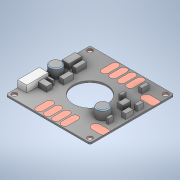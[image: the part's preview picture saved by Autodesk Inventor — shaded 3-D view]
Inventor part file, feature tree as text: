
AUTODESK INVENTOR PART (.ipt)
format: ipt  version: 2020 (Build 240168000, 168)  size: 288,256 bytes
history: mixed  units: in
note: dims shown in document units (in); Inventor stores cm internally (conversion verified against a paired STEP export)
features: other x13, chamfer x6, fillet x2, imported_body x1
ambient origin geometry x8: Origin, YZ Plane, XZ Plane, XY Plane, X Axis, Y Axis, Z Axis, Center Point
bodies: Solid1 (imported_parasolid), Solid2 (imported_parasolid), Solid3 (imported_parasolid), Solid4 (imported_parasolid), Solid5 (imported_parasolid), Solid6 (imported_parasolid), Solid7 (imported_parasolid), Solid8 (imported_parasolid), Solid9 (imported_parasolid), Solid10 (imported_parasolid), Solid11 (imported_parasolid), Solid12 (imported_parasolid), Solid13 (imported_parasolid), Solid14 (imported_parasolid), Solid15 (imported_parasolid), Solid16 (imported_parasolid), Solid17 (imported_parasolid), Solid18 (imported_parasolid), Solid19 (imported_parasolid), Solid20 (imported_parasolid), Solid21 (imported_parasolid)
feature tree (22):
  other  "Split Line4"
  fillet  "Fillet2"  [1 undecoded]
  fillet  "Fillet3"  [1 undecoded]
  other  "Boss-Extrude4[1]"
  other  "Boss-Extrude4[2]"
  other  "Boss-Extrude4[3]"
  other  "Boss-Extrude4[4]"
  other  "Boss-Extrude4[5]"
  other  "Boss-Extrude4[6]"
  other  "Boss-Extrude4[7]"
  other  "Boss-Extrude4[8]"
  other  "Boss-Extrude4[9]"
  other  "Boss-Extrude4[10]"
  other  "Boss-Extrude4[11]"
  other  "Cut-Extrude2"
  chamfer  "Chamfer1"  [1 undecoded]
  chamfer  "Chamfer2"  [1 undecoded]
  chamfer  "Chamfer3"  [1 undecoded]
  chamfer  "Chamfer4"  [1 undecoded]
  chamfer  "Chamfer5"  [1 undecoded]
  chamfer  "Chamfer6"  [1 undecoded]
  imported_body  NMx_Import_Brep_tag  [imported B-rep: ~180 faces, bbox_mm=[50.0, 6.5, 50.0]]
note: 8 required parameter values undecoded (feature->parameter linkage not recoverable at this tier; creation-order binding heuristic only, values carry confidence <= 0.55)
